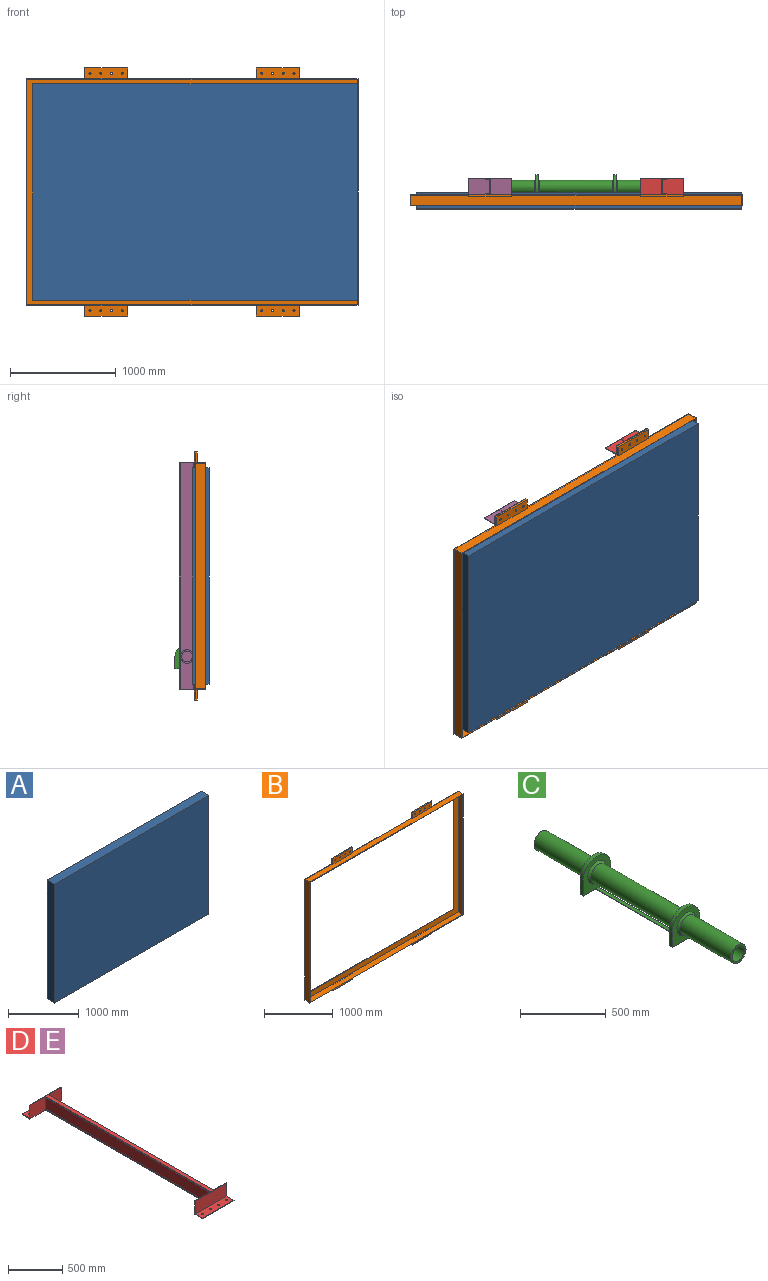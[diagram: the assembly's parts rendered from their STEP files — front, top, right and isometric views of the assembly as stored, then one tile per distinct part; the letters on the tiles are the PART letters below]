
ASSEMBLY  parts=5 mates=3
PART A: 6 faces, bbox 3072x155x2048 mm
  f0: plane 3072x154.99mm, normal (0,0,1), area 476132.2mm2, adj f1,f3,f4,f5
  f1: plane 2048x154.99mm, normal (-1,0,0), area 317421.5mm2, adj f0,f2,f4,f5
  f2: plane 3072x154.99mm, normal (0,0,-1), area 476132.2mm2, adj f1,f3,f4,f5
  f3: plane 2048x154.99mm, normal (1,0,0), area 317421.5mm2, adj f0,f2,f4,f5
  f4: plane 3072x2048mm, normal (0,-1,0), area 6291468.3mm2, adj f0,f1,f2,f3
  f5: plane 3072x2048mm, normal (0,1,0), area 6291468.3mm2, adj f0,f1,f2,f3
PART B: 47 faces, bbox 3141.6x101.6x2347.9 mm
  f0: plane 3141.64x2347.89mm, normal (0,1,0), area 1193493mm2, adj f4,f6,f7,f9,f10,f12,f13,f17
  f1: plane 406.4x101.6mm, normal (0,-1,0), area 40150.1mm2, adj f10,f22,f23,f24,f39,f40,f41,f42
  f2: plane 406.4x101.6mm, normal (0,-1,0), area 40150.1mm2, adj f7,f25,f26,f27,f35,f36,f37,f38
  f3: plane 406.4x101.6mm, normal (0,-1,0), area 40150.1mm2, adj f7,f28,f29,f30,f31,f32,f33,f34
  f4: plane 2144.69x101.6mm, normal (-1,0,0), area 217900.6mm2, adj f0,f7,f10,f14
  f5: plane 2131.99x95.25mm, normal (1,0,0), area 203072.1mm2, adj f8,f11,f14,f16
  f6: plane 1941.49x6.35mm, normal (1,0,0), area 12328.5mm2, adj f0,f9,f12,f16
  f7: plane 3141.64x101.6mm, normal (0,0,-1), area 303706.9mm2, adj f0,f2,f3,f4,f13,f14,f25,f27
  f8: plane 3128.94x95.25mm, normal (0,0,1), area 298031.6mm2, adj f5,f14,f15,f16
  f9: plane 2938.44x6.35mm, normal (0,0,1), area 18659.1mm2, adj f0,f6,f16,f17
  f10: plane 3141.64x101.6mm, normal (0,0,1), area 303706.9mm2, adj f0,f1,f4,f13,f14,f19,f20,f21
  f11: plane 3128.94x95.25mm, normal (0,0,-1), area 298031.6mm2, adj f5,f14,f15,f16
  f12: plane 2938.44x6.35mm, normal (0,0,-1), area 18659.1mm2, adj f0,f6,f16,f17
  f13: plane 2144.69x101.6mm, normal (1,0,0), area 217900.6mm2, adj f0,f7,f10,f14
  f14: plane 3141.64x2144.69mm, normal (0,-1,0), area 66975.1mm2, adj f4,f5,f7,f8,f10,f11,f13,f15
  f15: plane 2131.99x95.25mm, normal (-1,0,0), area 203072.1mm2, adj f8,f11,f14,f16
  f16: plane 3128.94x2131.99mm, normal (0,-1,0), area 965917.3mm2, adj f5,f6,f8,f9,f11,f12,f15,f17
  f17: plane 1941.49x6.35mm, normal (-1,0,0), area 12328.5mm2, adj f0,f9,f12,f16
  f18: plane 406.4x19.05mm, normal (0,0,1), area 7741.9mm2, adj f0,f19,f20,f21
  f19: plane 101.6x19.05mm, normal (1,0,0), area 1935.5mm2, adj f0,f10,f18,f21
  f20: plane 101.6x19.05mm, normal (-1,0,0), area 1935.5mm2, adj f0,f10,f18,f21
  f21: plane 406.4x101.6mm, normal (0,-1,0), area 40150.1mm2, adj f10,f18,f19,f20,f43,f44,f45,f46
  f22: plane 406.4x19.05mm, normal (0,0,1), area 7741.9mm2, adj f0,f1,f23,f24
  f23: plane 101.6x19.05mm, normal (1,0,0), area 1935.5mm2, adj f0,f1,f10,f22
  f24: plane 101.6x19.05mm, normal (-1,0,0), area 1935.5mm2, adj f0,f1,f10,f22
  f25: plane 101.6x19.05mm, normal (1,0,0), area 1935.5mm2, adj f0,f2,f7,f26
  f26: plane 406.4x19.05mm, normal (0,0,-1), area 7741.9mm2, adj f0,f2,f25,f27
  f27: plane 101.6x19.05mm, normal (-1,0,0), area 1935.5mm2, adj f0,f2,f7,f26
  f28: plane 406.4x19.05mm, normal (0,0,-1), area 7741.9mm2, adj f0,f3,f29,f30
  f29: plane 101.6x19.05mm, normal (-1,0,0), area 1935.5mm2, adj f0,f3,f7,f28
  f30: plane 101.6x19.05mm, normal (1,0,0), area 1935.5mm2, adj f0,f3,f7,f28
  f31: cylinder r=9.53mm len=19.05mm, axis (0,1,0), area 1140.1mm2, adj f0,f3
  f32: cylinder r=9.53mm len=19.05mm, axis (0,1,0), area 1140.1mm2, adj f0,f3
  f33: cylinder r=9.53mm len=19.05mm, axis (0,1,0), area 1140.1mm2, adj f0,f3
  f34: cylinder r=9.53mm len=19.05mm, axis (0,1,0), area 1140.1mm2, adj f0,f3
  f35: cylinder r=9.53mm len=19.05mm, axis (0,1,0), area 1140.1mm2, adj f0,f2
  f36: cylinder r=9.53mm len=19.05mm, axis (0,1,0), area 1140.1mm2, adj f0,f2
  f37: cylinder r=9.53mm len=19.05mm, axis (0,1,0), area 1140.1mm2, adj f0,f2
  f38: cylinder r=9.53mm len=19.05mm, axis (0,1,0), area 1140.1mm2, adj f0,f2
  f39: cylinder r=9.53mm len=19.05mm, axis (0,1,0), area 1140.1mm2, adj f0,f1
  f40: cylinder r=9.53mm len=19.05mm, axis (0,1,0), area 1140.1mm2, adj f0,f1
  f41: cylinder r=9.53mm len=19.05mm, axis (0,1,0), area 1140.1mm2, adj f0,f1
  f42: cylinder r=9.53mm len=19.05mm, axis (0,1,0), area 1140.1mm2, adj f0,f1
  f43: cylinder r=9.53mm len=19.05mm, axis (0,1,0), area 1140.1mm2, adj f0,f21
  f44: cylinder r=9.53mm len=19.05mm, axis (0,1,0), area 1140.1mm2, adj f0,f21
  f45: cylinder r=9.53mm len=19.05mm, axis (0,1,0), area 1140.1mm2, adj f0,f21
  f46: cylinder r=9.53mm len=19.05mm, axis (0,1,0), area 1140.1mm2, adj f0,f21
PART C: 25 faces, bbox 228.6x1625.6x228.6 mm
  f0: plane 228.6x228.6mm, normal (0,1,0), area 28344.6mm2, adj f7,f8,f9,f10,f20,f22,f23,f24
  f1: plane 228.6x228.6mm, normal (0,-1,0), area 28344.6mm2, adj f10,f12,f13,f14,f19,f22,f23,f24
  f2: cylinder r=63.5mm len=685.8mm, axis (0,1,0), area 273622mm2, adj f19,f20
  f3: cylinder r=63.5mm len=419.1mm, axis (0,1,0), area 167213.5mm2, adj f4,f18
  f4: plane 127x127mm, normal (0,-1,0), area 4560.4mm2, adj f3,f5
  f5: cylinder r=50.8mm len=1612.9mm, axis (0,1,0), area 514814.8mm2, adj f4,f6
  f6: plane 101.6x101.6mm, normal (0,-1,0), area 8107.3mm2, adj f5
  f7: plane 114.3x25.4mm, normal (1,0,0), area 2903.2mm2, adj f0,f8,f10,f11
  f8: cylinder r=114.3mm len=228.6mm, axis (0,-1,0), area 9120.7mm2, adj f0,f7,f9,f11
  f9: plane 114.3x25.4mm, normal (-1,0,0), area 2903.2mm2, adj f0,f8,f10,f11
  f10: plane 762x228.6mm, normal (0,0,-1), area 29677.4mm2, adj f0,f1,f7,f9,f11,f12,f13,f15
  f11: plane 228.6x228.6mm, normal (0,-1,0), area 28409.2mm2, adj f7,f8,f9,f10,f18
  f12: plane 114.3x25.4mm, normal (1,0,0), area 2903.2mm2, adj f1,f10,f14,f15
  f13: plane 114.3x25.4mm, normal (-1,0,0), area 2903.2mm2, adj f1,f10,f14,f15
  f14: cylinder r=114.3mm len=228.6mm, axis (0,1,0), area 9120.7mm2, adj f1,f12,f13,f15
  f15: plane 228.6x228.6mm, normal (0,1,0), area 28409.2mm2, adj f10,f12,f13,f14,f21
  f16: plane 127x127mm, normal (0,1,0), area 12667.7mm2, adj f17
  f17: cylinder r=63.5mm len=419.1mm, axis (0,1,0), area 167213.5mm2, adj f16,f21
  f18: cone r=63.5mm half-angle=45deg, axis (0,1,0), area 7882.5mm2, adj f3,f11
  f19: cone r=76.2mm half-angle=45deg, axis (0,1,0), area 7882.5mm2, adj f1,f2
  f20: cone r=76.2mm half-angle=45deg, axis (0,-1,0), area 7882.5mm2, adj f0,f2
  f21: cone r=76.2mm half-angle=45deg, axis (0,-1,0), area 7882.5mm2, adj f15,f17
  f22: plane 711.2x2.54mm, normal (1,0,0), area 1806.4mm2, adj f0,f1,f10,f24
  f23: plane 711.2x2.54mm, normal (-1,0,0), area 1806.4mm2, adj f0,f1,f10,f24
  f24: plane 711.2x25.4mm, normal (0,0,1), area 18064.5mm2, adj f0,f1,f22,f23
PART D: 32 faces, bbox 406.4x2347.9x152.4 mm
  f0: plane 2347.87x406.4mm, normal (0,0,-1), area 166955.3mm2, adj f5,f6,f10,f11,f14,f15,f16,f17
  f1: cylinder r=6.35mm len=2144.67mm, axis (0,1,0), area 21392.2mm2, adj f2,f9,f11,f18
  f2: plane 2144.67x29.21mm, normal (0,0,-1), area 62645.9mm2, adj f1,f3,f11,f18
  f3: plane 2144.67x7.52mm, normal (1,0,0), area 16124.5mm2, adj f2,f4,f11,f18
  f4: plane 2157.37x406.4mm, normal (0,0,1), area 91449.3mm2, adj f3,f5,f10,f11,f12,f15,f16,f17
  f5: plane 2144.67x152.4mm, normal (-1,0,0), area 326848.4mm2, adj f0,f4,f10,f17
  f6: plane 2144.67x7.52mm, normal (1,0,0), area 16124.5mm2, adj f0,f7,f11,f18
  f7: plane 2144.67x29.21mm, normal (0,0,1), area 62645.9mm2, adj f6,f8,f11,f18
  f8: cylinder r=6.35mm len=2144.67mm, axis (0,1,0), area 21392.2mm2, adj f7,f9,f11,f18
  f9: plane 2144.67x124.66mm, normal (1,0,0), area 267362mm2, adj f1,f8,f11,f18
  f10: plane 203.2x152.4mm, normal (0,-1,0), area 30967.7mm2, adj f0,f4,f5,f15
  f11: plane 198.53x152.4mm, normal (0,-1,0), area 29703.4mm2, adj f0,f1,f2,f3,f4,f6,f7,f8
  f12: plane 406.4x146.05mm, normal (0,1,0), area 59354.7mm2, adj f4,f13,f15,f16
  f13: plane 406.4x95.25mm, normal (0,0,1), area 37753mm2, adj f12,f14,f15,f16,f28,f29,f30,f31
  f14: plane 406.4x6.35mm, normal (0,1,0), area 2580.6mm2, adj f0,f13,f15,f16
  f15: plane 152.4x101.6mm, normal (-1,0,0), area 1572.6mm2, adj f0,f4,f10,f12,f13,f14
  f16: plane 152.4x101.6mm, normal (1,0,0), area 1572.6mm2, adj f0,f4,f11,f12,f13,f14
  f17: plane 203.2x152.4mm, normal (0,1,0), area 30967.7mm2, adj f0,f4,f5,f22
  f18: plane 198.53x152.4mm, normal (0,1,0), area 29703.4mm2, adj f0,f1,f2,f3,f4,f6,f7,f8
  f19: plane 406.4x6.35mm, normal (0,-1,0), area 2580.6mm2, adj f0,f20,f22,f23
  f20: plane 406.4x95.25mm, normal (0,0,1), area 37753mm2, adj f19,f21,f22,f23,f24,f25,f26,f27
  f21: plane 406.4x146.05mm, normal (0,-1,0), area 59354.7mm2, adj f4,f20,f22,f23
  f22: plane 152.4x101.6mm, normal (-1,0,0), area 1572.6mm2, adj f0,f4,f17,f19,f20,f21
  f23: plane 152.4x101.6mm, normal (1,0,0), area 1572.6mm2, adj f0,f4,f18,f19,f20,f21
  f24: cylinder r=8.72mm len=17.45mm, axis (0,0,-1), area 348.1mm2, adj f0,f20
  f25: cylinder r=8.72mm len=17.45mm, axis (0,0,-1), area 348.1mm2, adj f0,f20
  f26: cylinder r=8.72mm len=17.45mm, axis (0,0,-1), area 348.1mm2, adj f0,f20
  f27: cylinder r=8.72mm len=17.45mm, axis (0,0,-1), area 348.1mm2, adj f0,f20
  f28: cylinder r=8.72mm len=17.45mm, axis (0,0,-1), area 348.1mm2, adj f0,f13
  f29: cylinder r=8.72mm len=17.45mm, axis (0,0,-1), area 348.1mm2, adj f0,f13
  f30: cylinder r=8.72mm len=17.45mm, axis (0,0,-1), area 348.1mm2, adj f0,f13
  f31: cylinder r=8.72mm len=17.45mm, axis (0,0,-1), area 348.1mm2, adj f0,f13
PART E: same geometry as D
PLACE A t=(-920.81,-757.79,-1689.92)mm
PLACE B t=(-955.59,-781.31,-1322.57)mm
PLACE C rot(axis=(0,0,-1),90deg) t=(-949.28,-705.11,-2451.91)mm
PLACE D rot(axis=(-1,0,0),90deg) t=(-117.91,-727.85,-1689.91)mm
PLACE E rot(axis=(0,-0.71,-0.71),180deg) t=(-1780.66,-727.85,-1689.91)mm
MATE fastened E.f5 <-> C.f2  axis (1,0,0) through (-1762.08,-705.11,-2451.91)mm
MATE fastened C.f2 <-> D.f5  axis (1,0,0) through (-136.48,-705.11,-2451.91)mm
MATE fastened B.f44 <-> D.f25  axis (0,1,0) through (15.92,-781.31,-566.77)mm
